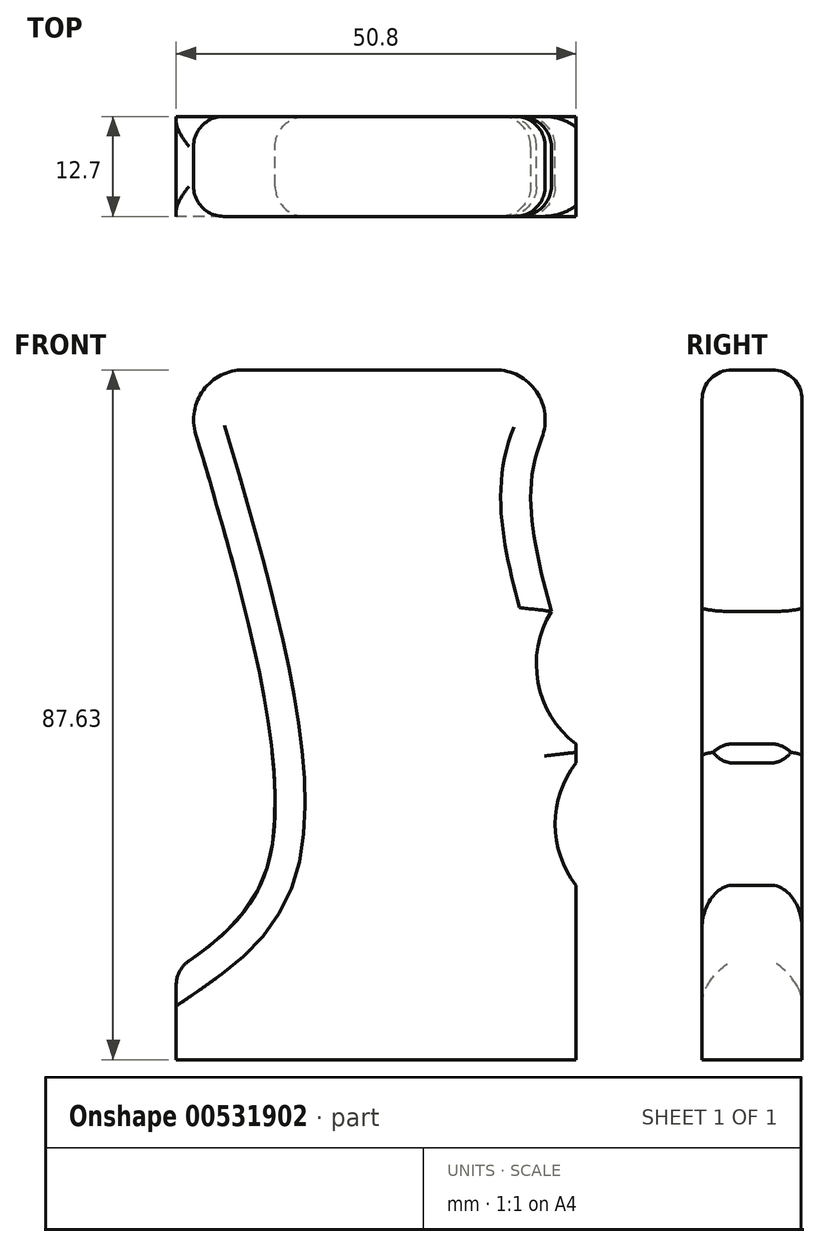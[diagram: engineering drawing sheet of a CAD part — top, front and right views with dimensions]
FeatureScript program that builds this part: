
annotation { "Feature Type Name" : "Feature", "Feature Type Description" : "" }
export const myFeature = defineFeature(function(context is Context, id is Id, definition is map)
    precondition{}
    {
        {
            var Q0;
            Q0=qCreatedBy(makeId("Front.planeOp"),FACE);
            var sketch = newSketch(context, id + "F0", { "sketchPlane" : qUnion([Q0])});
            skLineSegment(sketch, "E0.bottom", {"start": v(15.12, 38.1) * mm, "end": v(-16.84, 38.1) * mm});
            skLineSegment(sketch, "E0.top", {"start": v(25.4, -38.1) * mm, "end": v(-25.4, -38.1) * mm});
            skLineSegment(sketch, "E0.left", {"start": v(25.4, 38.1) * mm, "end": v(25.4, -38.1) * mm});
            skLineSegment(sketch, "E0.right", {"start": v(-25.4, 38.1) * mm, "end": v(-25.4, -38.1) * mm});
            skPoint(sketch, "E0.middle", {"position": v(0, 0) * mm});
            skFitSpline(sketch, "E1", {"points": [v(-25.4, -38.1) * mm, v(-13.68, -24.5) * mm, v(-25.4, 38.1) * mm], "startDerivative": vector(42.75, 29.4) * mm, "endDerivative": vector(-34.83, 114.32) * mm});
            skFitSpline(sketch, "E2", {"points": [v(25.4, -38.1) * mm, v(26.77, -10.33) * mm, v(19.65, 23) * mm, v(25.4, 38.1) * mm], "startDerivative": vector(14.76, 76.52) * mm, "endDerivative": vector(25.55, 50.57) * mm});
            skArc(sketch, "E3.filletArc", {"start": v(-16.84, 38.1) * mm, "mid": v(-21.93, 35.54) * mm, "end": v(-22.92, 29.92) * mm});
            skArc(sketch, "E4.filletArc", {"start": v(21.05, 29.48) * mm, "mid": v(20.36, 35.35) * mm, "end": v(15.12, 38.1) * mm});
            skLineSegment(sketch, "E5", {"start": v(19.05, -38.1) * mm, "end": v(19.05, 38.1) * mm});
            skArc(sketch, "E6", {"start": v(26.77, -10.33) * mm, "mid": v(22.73, -19.85) * mm, "end": v(27.12, -29.21) * mm});
            skArc(sketch, "E7", {"start": v(26.77, 11.74) * mm, "mid": v(20.35, 0.7) * mm, "end": v(26.77, -10.33) * mm});
            skLineSegment(sketch, "E8.bottom", {"start": v(-25.4, -38.1) * mm, "end": v(25.4, -38.1) * mm});
            skLineSegment(sketch, "E8.top", {"start": v(-25.4, -49.53) * mm, "end": v(25.4, -49.53) * mm});
            skLineSegment(sketch, "E8.left", {"start": v(-25.4, -38.1) * mm, "end": v(-25.4, -49.53) * mm});
            skLineSegment(sketch, "E8.right", {"start": v(25.4, -38.1) * mm, "end": v(25.4, -49.53) * mm});
            skSolve(sketch);
        }
        {
            var Q0;
            Q0=makeQuery(id+"F0.imprint","IMPRINT",FACE,{"disambiguationData":[TD([[makeQuery(id+"F0.imprint","IMPRINT",EDGE,{"derivedFrom":sQuery(id+"F0.wireOp",EDGE,"E0.bottom")}),1.0]])]});
            var Q1;
            {var subQ3=sQuery(id+"F0.wireOp",EDGE,"E7");var subQ5=sQuery(id+"F0.wireOp",EDGE,"E0.left");var subQ10=makeQuery(id+"F0.imprint","INTERSECT",VERTEX,{"disambiguationData":[OD(1.0)],"derivedFrom":[subQ5,subQ3]});Q1=makeQuery(id+"F0.imprint","IMPRINT",FACE,{"disambiguationData":[TD([[makeQuery(id+"F0.imprint","IMPRINT",EDGE,{"disambiguationData":[TD([[subQ10,-1.0]])],"derivedFrom":subQ5}),-1.0]])]});}
            var Q2;
            Q2=makeQuery(id+"F0.imprint","IMPRINT",FACE,{"disambiguationData":[TD([[makeQuery(id+"F0.imprint","IMPRINT",EDGE,{"derivedFrom":sQuery(id+"F0.wireOp",EDGE,"E8.top")}),1.0]])]});
            extrude(context, id + "F1", {"entities" : qUnion([Q0, Q1, Q2]), "depth" : 12.7 * mm, "offsetDistance" : 25.4 * mm});
        }
        {
            var Q0;
            Q0=makeQuery(id+"F1.opExtrude","SWEPT_FACE",FACE,{"disambiguationData":[OSD([sQuery(id+"F0.wireOp",EDGE,"E1")])]});
            var Q1;
            Q1=makeQuery(id+"F1.opExtrude","CAP_EDGE",EDGE,{"disambiguationData":[OSD([sQuery(id+"F0.wireOp",EDGE,"E7")])],"isStart":true});
            var Q2;
            Q2=makeQuery(id+"F1.opExtrude","CAP_EDGE",EDGE,{"disambiguationData":[OSD([sQuery(id+"F0.wireOp",EDGE,"E6")])],"isStart":true});
            var Q3;
            Q3=makeQuery(id+"F1.opExtrude","CAP_EDGE",EDGE,{"disambiguationData":[OSD([sQuery(id+"F0.wireOp",EDGE,"E6")])],"isStart":false});
            var Q4;
            Q4=makeQuery(id+"F1.opExtrude","CAP_EDGE",EDGE,{"disambiguationData":[OSD([sQuery(id+"F0.wireOp",EDGE,"E7")])],"isStart":false});
            fillet(context, id + "F2", {"entities" : qUnion([Q0, Q1, Q2, Q3, Q4]), "radius" : 3.8 * mm, "tangentPropagation" : true, "allowEdgeOverflow" : false});
        }
    });
